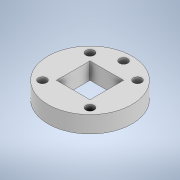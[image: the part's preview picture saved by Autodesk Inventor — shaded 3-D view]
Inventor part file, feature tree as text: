
AUTODESK INVENTOR PART (.ipt)
format: ipt  version: 2022.3 (Build 263350000, 350)  size: 125,952 bytes
history: native  units: in
note: dims shown in document units (in); Inventor stores cm internally (conversion verified against a paired STEP export)
features: extrude x1, sketch x1
ambient origin geometry x8: Origin, YZ Plane, XZ Plane, XY Plane, X Axis, Y Axis, Z Axis, Center Point
bodies: Solid1 (feature_tree)
feature tree (2):
  extrude  "Extrusion1"  Depth=0.7874in
  sketch  "Sketch1"  dims[d0=0.7874in d1=0.7874in d2=135.0deg d3=0.1969in d4=0.1969in d5=0.7874in d6=90.0deg d7=0.1969in d8=0.7874in d9=90.0deg d10=0.1969in d11=0.7874in d12=90.0deg d13=0.1969in d14=0.7874in d15=0.7874in d16=0.3937in d17=0.0in]
